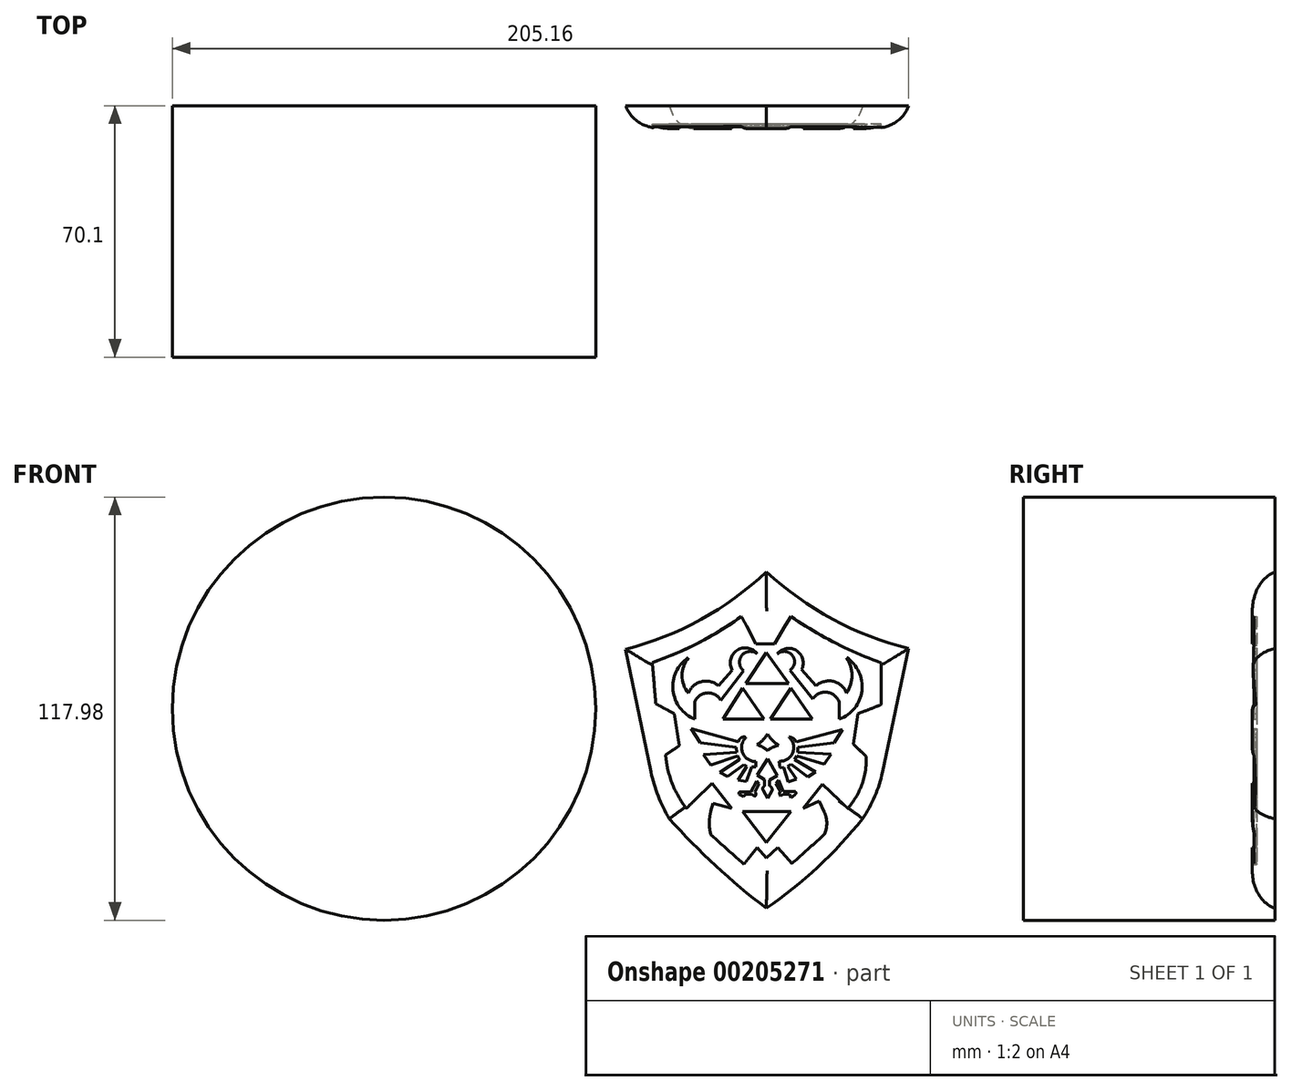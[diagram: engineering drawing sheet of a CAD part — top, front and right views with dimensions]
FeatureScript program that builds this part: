
annotation { "Feature Type Name" : "Feature", "Feature Type Description" : "" }
export const myFeature = defineFeature(function(context is Context, id is Id, definition is map)
    precondition{}
    {
        {
            var Q0;
            Q0=qCreatedBy(makeId("Front.planeOp"),FACE);
            var sketch = newSketch(context, id + "F0", { "sketchPlane" : qUnion([Q0])});
            skArc(sketch, "E0", {"start": v(0, 38.14) * mm, "mid": v(18.47, 24.95) * mm, "end": v(39.64, 16.77) * mm});
            skArc(sketch, "E1", {"start": v(-39.2, 16.56) * mm, "mid": v(-18.22, 24.85) * mm, "end": v(0, 38.14) * mm});
            skLineSegment(sketch, "E2", {"start": v(39.64, 16.77) * mm, "end": v(32.38, -17.63) * mm});
            skArc(sketch, "E3", {"start": v(26.82, -30.66) * mm, "mid": v(30.24, -24.41) * mm, "end": v(32.38, -17.63) * mm});
            skLineSegment(sketch, "E4", {"start": v(-39.2, 16.56) * mm, "end": v(-32.14, -17.63) * mm});
            skArc(sketch, "E5", {"start": v(-32.14, -17.63) * mm, "mid": v(-30.14, -24.36) * mm, "end": v(-27.02, -30.66) * mm});
            skArc(sketch, "E6", {"start": v(-27.02, -30.66) * mm, "mid": v(-14.13, -43.82) * mm, "end": v(0, -55.62) * mm});
            skArc(sketch, "E7", {"start": v(0, -55.62) * mm, "mid": v(14.35, -44.15) * mm, "end": v(26.82, -30.66) * mm});
            skLineSegment(sketch, "E8", {"start": v(0, 15.6) * mm, "end": v(6.22, 7.02) * mm});
            skLineSegment(sketch, "E9", {"start": v(6.22, 7.02) * mm, "end": v(-5.68, 7.02) * mm});
            skLineSegment(sketch, "E10", {"start": v(-5.68, 7.02) * mm, "end": v(0, 15.6) * mm});
            skLineSegment(sketch, "E11", {"start": v(6.82, 5.71) * mm, "end": v(12.77, -2.86) * mm});
            skLineSegment(sketch, "E12", {"start": v(12.77, -2.86) * mm, "end": v(1.18, -2.86) * mm});
            skLineSegment(sketch, "E13", {"start": v(1.18, -2.86) * mm, "end": v(6.82, 5.71) * mm});
            skLineSegment(sketch, "E14", {"start": v(-6.59, 5.71) * mm, "end": v(-0.64, -2.86) * mm});
            skLineSegment(sketch, "E15", {"start": v(-0.64, -2.86) * mm, "end": v(-12.03, -2.86) * mm});
            skLineSegment(sketch, "E16", {"start": v(-12.03, -2.86) * mm, "end": v(-6.59, 5.71) * mm});
            skLineSegment(sketch, "E17", {"start": v(6.82, -28.67) * mm, "end": v(0, -37.27) * mm});
            skLineSegment(sketch, "E18", {"start": v(0, -37.27) * mm, "end": v(-6.59, -28.67) * mm});
            skLineSegment(sketch, "E19", {"start": v(-6.59, -28.67) * mm, "end": v(6.82, -28.67) * mm});
            skArc(sketch, "E20", {"start": v(0.3, -7.06) * mm, "mid": v(1.7, -8.83) * mm, "end": v(3.44, -10.24) * mm});
            skArc(sketch, "E21", {"start": v(3.44, -10.24) * mm, "mid": v(1.8, -10.76) * mm, "end": v(0.3, -11.64) * mm});
            skArc(sketch, "E22", {"start": v(0.3, -11.64) * mm, "mid": v(-1.07, -10.72) * mm, "end": v(-2.6, -10.06) * mm});
            skArc(sketch, "E23", {"start": v(-2.6, -10.06) * mm, "mid": v(-0.95, -8.75) * mm, "end": v(0.3, -7.06) * mm});
            skArc(sketch, "E24", {"start": v(3.56, -14.66) * mm, "mid": v(7.35, -12.25) * mm, "end": v(6.28, -7.9) * mm});
            skLineSegment(sketch, "E25", {"start": v(3.56, -14.66) * mm, "end": v(3.83, -16.47) * mm});
            skLineSegment(sketch, "E26", {"start": v(3.83, -16.47) * mm, "end": v(4.79, -16.33) * mm});
            skLineSegment(sketch, "E27", {"start": v(4.79, -16.33) * mm, "end": v(6.13, -20.44) * mm});
            skLineSegment(sketch, "E28", {"start": v(6.13, -20.44) * mm, "end": v(8.33, -19.72) * mm});
            skLineSegment(sketch, "E29", {"start": v(8.33, -19.72) * mm, "end": v(5.9, -16.13) * mm});
            skLineSegment(sketch, "E30", {"start": v(5.9, -16.13) * mm, "end": v(6.88, -15.47) * mm});
            skLineSegment(sketch, "E31", {"start": v(6.88, -15.47) * mm, "end": v(11.5, -19) * mm});
            skLineSegment(sketch, "E32", {"start": v(11.5, -19) * mm, "end": v(13.74, -17.66) * mm});
            skLineSegment(sketch, "E33", {"start": v(13.74, -17.66) * mm, "end": v(7.9, -14.24) * mm});
            skLineSegment(sketch, "E34", {"start": v(7.9, -14.24) * mm, "end": v(8.55, -13.14) * mm});
            skLineSegment(sketch, "E35", {"start": v(8.55, -13.14) * mm, "end": v(16.18, -15.47) * mm});
            skLineSegment(sketch, "E36", {"start": v(16.18, -15.47) * mm, "end": v(18.03, -12.7) * mm});
            skLineSegment(sketch, "E37", {"start": v(18.03, -12.7) * mm, "end": v(8.78, -12.13) * mm});
            skLineSegment(sketch, "E38", {"start": v(8.78, -12.13) * mm, "end": v(8.78, -10.77) * mm});
            skLineSegment(sketch, "E39", {"start": v(8.78, -10.77) * mm, "end": v(18.97, -9.56) * mm});
            skLineSegment(sketch, "E40", {"start": v(18.97, -9.56) * mm, "end": v(21.16, -5.78) * mm});
            skLineSegment(sketch, "E41", {"start": v(21.16, -5.78) * mm, "end": v(8.33, -9.22) * mm});
            skArc(sketch, "E42", {"start": v(8.33, -9.22) * mm, "mid": v(7.48, -8.3) * mm, "end": v(6.28, -7.9) * mm});
            skLineSegment(sketch, "E43", {"start": v(0.4, -14) * mm, "end": v(3.07, -18.64) * mm});
            skLineSegment(sketch, "E44", {"start": v(3.07, -18.64) * mm, "end": v(0.93, -19.87) * mm});
            skLineSegment(sketch, "E45", {"start": v(0.93, -19.87) * mm, "end": v(0.93, -21.55) * mm});
            skLineSegment(sketch, "E46", {"start": v(0.4, -14) * mm, "end": v(-2.5, -18.52) * mm});
            skLineSegment(sketch, "E47", {"start": v(-2.5, -18.52) * mm, "end": v(-0.45, -19.84) * mm});
            skLineSegment(sketch, "E48", {"start": v(-0.45, -19.84) * mm, "end": v(-0.45, -21.55) * mm});
            skLineSegment(sketch, "E49", {"start": v(3.43, -19.87) * mm, "end": v(2.62, -20.77) * mm});
            skLineSegment(sketch, "E50", {"start": v(2.62, -20.77) * mm, "end": v(3.88, -22.96) * mm});
            skLineSegment(sketch, "E51", {"start": v(3.43, -19.87) * mm, "end": v(4.75, -23.1) * mm});
            skLineSegment(sketch, "E52", {"start": v(4.75, -23.1) * mm, "end": v(8.08, -23.1) * mm});
            skLineSegment(sketch, "E53", {"start": v(3.88, -24.34) * mm, "end": v(4.66, -23.83) * mm});
            skLineSegment(sketch, "E54", {"start": v(4.66, -23.83) * mm, "end": v(6.46, -23.83) * mm});
            skLineSegment(sketch, "E55", {"start": v(6.46, -23.83) * mm, "end": v(6.88, -24.82) * mm});
            skLineSegment(sketch, "E56", {"start": v(6.88, -24.82) * mm, "end": v(7.96, -24) * mm});
            skArc(sketch, "E57", {"start": v(7.96, -24) * mm, "mid": v(8.2, -23.58) * mm, "end": v(8.08, -23.1) * mm});
            skArc(sketch, "E58", {"start": v(1.58, -22.78) * mm, "mid": v(1.48, -22.04) * mm, "end": v(0.93, -21.55) * mm});
            skLineSegment(sketch, "E59", {"start": v(1.58, -22.78) * mm, "end": v(0.4, -25.04) * mm});
            skLineSegment(sketch, "E60", {"start": v(0.4, -25.04) * mm, "end": v(-0.9, -22.78) * mm});
            skArc(sketch, "E61", {"start": v(-0.45, -21.55) * mm, "mid": v(-0.96, -22.06) * mm, "end": v(-0.9, -22.78) * mm});
            skArc(sketch, "E62", {"start": v(-5.7, -7.99) * mm, "mid": v(-6.6, -12.34) * mm, "end": v(-2.89, -14.76) * mm});
            skArc(sketch, "E63", {"start": v(-5.7, -7.99) * mm, "mid": v(-7.02, -8.13) * mm, "end": v(-7.74, -9.24) * mm});
            skLineSegment(sketch, "E64", {"start": v(-2.89, -14.76) * mm, "end": v(-2.89, -16.26) * mm});
            skPoint(sketch, "E64.endSnap0", {"position": v(-1.05, -16.26) * mm});
            skLineSegment(sketch, "E65", {"start": v(-2.89, -16.26) * mm, "end": v(-4.14, -16.26) * mm});
            skLineSegment(sketch, "E66", {"start": v(-4.14, -16.26) * mm, "end": v(-5.63, -20.36) * mm});
            skLineSegment(sketch, "E67", {"start": v(-5.63, -20.36) * mm, "end": v(-7.88, -19.9) * mm});
            skLineSegment(sketch, "E68", {"start": v(-7.88, -19.9) * mm, "end": v(-5.41, -16.05) * mm});
            skLineSegment(sketch, "E69", {"start": v(-5.41, -16.05) * mm, "end": v(-6.2, -15.55) * mm});
            skLineSegment(sketch, "E70", {"start": v(-6.2, -15.55) * mm, "end": v(-10.77, -18.93) * mm});
            skLineSegment(sketch, "E71", {"start": v(-10.77, -18.93) * mm, "end": v(-13.01, -17.83) * mm});
            skLineSegment(sketch, "E72", {"start": v(-13.01, -17.83) * mm, "end": v(-7.45, -14.2) * mm});
            skLineSegment(sketch, "E73", {"start": v(-7.99, -13.16) * mm, "end": v(-15.54, -15.72) * mm});
            skLineSegment(sketch, "E74", {"start": v(-15.54, -15.72) * mm, "end": v(-17.58, -12.87) * mm});
            skLineSegment(sketch, "E75", {"start": v(-17.58, -12.87) * mm, "end": v(-8.27, -12.16) * mm});
            skLineSegment(sketch, "E76", {"start": v(-8.27, -12.16) * mm, "end": v(-8.38, -10.8) * mm});
            skLineSegment(sketch, "E77", {"start": v(-8.38, -10.8) * mm, "end": v(-18.4, -9.56) * mm});
            skLineSegment(sketch, "E78", {"start": v(-18.4, -9.56) * mm, "end": v(-20.97, -5.62) * mm});
            skLineSegment(sketch, "E79", {"start": v(-20.97, -5.62) * mm, "end": v(-7.74, -9.24) * mm});
            skArc(sketch, "E80", {"start": v(-7.99, -13.16) * mm, "mid": v(-7.75, -13.69) * mm, "end": v(-7.45, -14.2) * mm});
            skLineSegment(sketch, "E81", {"start": v(-2.69, -20.14) * mm, "end": v(-2.05, -20.98) * mm});
            skLineSegment(sketch, "E82", {"start": v(-2.05, -20.98) * mm, "end": v(-3.22, -23.19) * mm});
            skLineSegment(sketch, "E83", {"start": v(-2.69, -20.14) * mm, "end": v(-4.3, -23.19) * mm});
            skLineSegment(sketch, "E84", {"start": v(-4.3, -23.19) * mm, "end": v(-7.2, -23.19) * mm});
            skArc(sketch, "E85", {"start": v(-3.22, -24.52) * mm, "mid": v(-2.93, -23.86) * mm, "end": v(-3.22, -23.19) * mm});
            skLineSegment(sketch, "E86", {"start": v(-3.22, -24.52) * mm, "end": v(-4.09, -23.86) * mm});
            skLineSegment(sketch, "E87", {"start": v(-4.09, -23.86) * mm, "end": v(-5.74, -23.86) * mm});
            skLineSegment(sketch, "E88", {"start": v(-5.74, -23.86) * mm, "end": v(-6.42, -24.52) * mm});
            skLineSegment(sketch, "E89", {"start": v(-6.42, -24.52) * mm, "end": v(-7.6, -23.86) * mm});
            skArc(sketch, "E90", {"start": v(3.88, -22.96) * mm, "mid": v(3.7, -23.65) * mm, "end": v(3.88, -24.34) * mm});
            skArc(sketch, "E91", {"start": v(-7.2, -23.19) * mm, "mid": v(-7.6, -23.4) * mm, "end": v(-7.6, -23.86) * mm});
            skLineSegment(sketch, "E92", {"start": v(-6.96, 25.7) * mm, "end": v(-2.88, 18.02) * mm});
            skLineSegment(sketch, "E93", {"start": v(-2.88, 18.02) * mm, "end": v(2.28, 18.02) * mm});
            skLineSegment(sketch, "E94", {"start": v(2.28, 18.02) * mm, "end": v(6.83, 25.7) * mm});
            skArc(sketch, "E95", {"start": v(6.83, 25.7) * mm, "mid": v(19, 18.4) * mm, "end": v(32.01, 12.75) * mm});
            skLineSegment(sketch, "E96", {"start": v(32.01, 12.75) * mm, "end": v(32.01, 1.12) * mm});
            skLineSegment(sketch, "E97", {"start": v(32.01, 1.12) * mm, "end": v(25.54, -1.4) * mm});
            skLineSegment(sketch, "E98", {"start": v(25.54, -1.4) * mm, "end": v(24.22, -9.91) * mm});
            skLineSegment(sketch, "E99", {"start": v(24.22, -9.91) * mm, "end": v(27.82, -13.27) * mm});
            skArc(sketch, "E100", {"start": v(-31.78, 12.87) * mm, "mid": v(-18.89, 18.36) * mm, "end": v(-6.96, 25.7) * mm});
            skLineSegment(sketch, "E101", {"start": v(-31.78, 12.87) * mm, "end": v(-30.82, 1.36) * mm});
            skLineSegment(sketch, "E102", {"start": v(-30.82, 1.36) * mm, "end": v(-25.66, -1.4) * mm});
            skLineSegment(sketch, "E103", {"start": v(-25.66, -1.4) * mm, "end": v(-24.22, -10.27) * mm});
            skLineSegment(sketch, "E104", {"start": v(-24.22, -10.27) * mm, "end": v(-28.06, -12.91) * mm});
            skArc(sketch, "E105", {"start": v(-28.06, -12.91) * mm, "mid": v(-26.28, -20.77) * mm, "end": v(-22.3, -27.78) * mm});
            skArc(sketch, "E106", {"start": v(22.66, -27.78) * mm, "mid": v(26.65, -21.03) * mm, "end": v(27.82, -13.27) * mm});
            skLineSegment(sketch, "E107", {"start": v(22.66, -27.78) * mm, "end": v(15.59, -21.06) * mm});
            skLineSegment(sketch, "E108", {"start": v(15.59, -21.06) * mm, "end": v(10.3, -27.78) * mm});
            skLineSegment(sketch, "E109", {"start": v(10.3, -27.78) * mm, "end": v(14.75, -25.74) * mm});
            skLineSegment(sketch, "E110", {"start": v(14.75, -25.74) * mm, "end": v(16.14, -28.77) * mm});
            skLineSegment(sketch, "E111", {"start": v(-22.3, -27.78) * mm, "end": v(-15.11, -20.83) * mm});
            skLineSegment(sketch, "E112", {"start": v(-15.11, -20.83) * mm, "end": v(-9.6, -27.78) * mm});
            skLineSegment(sketch, "E113", {"start": v(-9.6, -27.78) * mm, "end": v(-14.84, -26.35) * mm});
            skLineSegment(sketch, "E114", {"start": v(-14.84, -26.35) * mm, "end": v(-15.46, -28.6) * mm});
            skArc(sketch, "E115", {"start": v(-15.46, -28.6) * mm, "mid": v(-15.9, -31.89) * mm, "end": v(-15.46, -35.17) * mm});
            skArc(sketch, "E116", {"start": v(16.14, -35.1) * mm, "mid": v(16.83, -31.93) * mm, "end": v(16.14, -28.77) * mm});
            skLineSegment(sketch, "E117", {"start": v(16.14, -35.1) * mm, "end": v(7.15, -43.16) * mm});
            skLineSegment(sketch, "E118", {"start": v(7.15, -43.16) * mm, "end": v(3.2, -38.75) * mm});
            skLineSegment(sketch, "E119", {"start": v(3.2, -38.75) * mm, "end": v(0, -41.61) * mm});
            skLineSegment(sketch, "E120", {"start": v(0, -41.61) * mm, "end": v(-2.57, -38.75) * mm});
            skLineSegment(sketch, "E121", {"start": v(-2.57, -38.75) * mm, "end": v(-6.26, -43.37) * mm});
            skLineSegment(sketch, "E122", {"start": v(-6.26, -43.37) * mm, "end": v(-15.46, -35.17) * mm});
            skPoint(sketch, "E123.endSnap0", {"position": v(-12.36, -24.3) * mm});
            skLineSegment(sketch, "E124", {"start": v(-9.5, 10.75) * mm, "end": v(-13.34, 6.35) * mm});
            skLineSegment(sketch, "E125", {"start": v(9.82, 10.9) * mm, "end": v(13.88, 6.35) * mm});
            skLineSegment(sketch, "E126", {"start": v(6.56, 10.64) * mm, "end": v(12.9, 2.63) * mm});
            skLineSegment(sketch, "E127", {"start": v(20.34, 1.56) * mm, "end": v(20.34, -2.92) * mm});
            skLineSegment(sketch, "E128", {"start": v(-19.93, 1.94) * mm, "end": v(-19.93, -2.92) * mm});
            skLineSegment(sketch, "E129", {"start": v(-6.3, 10.54) * mm, "end": v(-12.72, 2.36) * mm});
            skArc(sketch, "E130", {"start": v(-12.72, 2.36) * mm, "mid": v(-16.46, 4.4) * mm, "end": v(-19.93, 1.94) * mm});
            skArc(sketch, "E131", {"start": v(-13.34, 6.35) * mm, "mid": v(-18.08, 7.52) * mm, "end": v(-21.74, 4.29) * mm});
            skArc(sketch, "E132", {"start": v(-21.74, 14.22) * mm, "mid": v(-23.49, 9.25) * mm, "end": v(-21.74, 4.29) * mm});
            skArc(sketch, "E133", {"start": v(-21.74, 14.22) * mm, "mid": v(-26, 5.1) * mm, "end": v(-19.93, -2.92) * mm});
            skArc(sketch, "E134", {"start": v(22.37, 4.29) * mm, "mid": v(18.68, 7.59) * mm, "end": v(13.88, 6.35) * mm});
            skArc(sketch, "E135", {"start": v(20.34, 1.56) * mm, "mid": v(16.97, 4.53) * mm, "end": v(12.9, 2.63) * mm});
            skArc(sketch, "E136", {"start": v(22.37, 4.29) * mm, "mid": v(23.83, 9.25) * mm, "end": v(22.37, 14.22) * mm});
            skArc(sketch, "E137", {"start": v(20.34, -2.92) * mm, "mid": v(26.6, 5.03) * mm, "end": v(22.37, 14.22) * mm});
            skArc(sketch, "E138", {"start": v(9.82, 10.9) * mm, "mid": v(8.44, 16.14) * mm, "end": v(3.1, 15.29) * mm});
            skArc(sketch, "E139", {"start": v(6.56, 10.64) * mm, "mid": v(7.27, 14.8) * mm, "end": v(3.1, 15.29) * mm});
            skArc(sketch, "E140", {"start": v(-2.57, 15.29) * mm, "mid": v(-6.85, 14.8) * mm, "end": v(-6.3, 10.54) * mm});
            skArc(sketch, "E141", {"start": v(-2.57, 15.29) * mm, "mid": v(-8.16, 16.26) * mm, "end": v(-9.5, 10.75) * mm});
            skCircle(sketch, "E142", {"center": v(-106.54, 0) * mm, "radius": 58.99 * mm});
            skSolve(sketch);
        }
        {
            var Q0;
            Q0=makeQuery(id+"F0.imprint","IMPRINT",FACE,{"disambiguationData":[TD([[makeQuery(id+"F0.imprint","IMPRINT",EDGE,{"derivedFrom":sQuery(id+"F0.wireOp",EDGE,"E0")}),-1.0]])]});
            extrude(context, id + "F1", {"entities" : qUnion([Q0]), "depth" : 6.35 * mm});
        }
        {
            var Q0;
            Q0=makeQuery(id+"F0.imprint","IMPRINT",FACE,{"disambiguationData":[TD([[makeQuery(id+"F0.imprint","IMPRINT",EDGE,{"derivedFrom":sQuery(id+"F0.wireOp",EDGE,"E8")}),1.0]])]});
            extrude(context, id + "F2", {"entities" : qUnion([Q0]), "operationType" : NewBodyOperationType.ADD, "depth" : 5.08 * mm});
        }
        {
            var Q0;
            Q0=makeQuery(id+"F0.imprint","IMPRINT",FACE,{"disambiguationData":[TD([[makeQuery(id+"F0.imprint","IMPRINT",EDGE,{"derivedFrom":sQuery(id+"F0.wireOp",EDGE,"E11")}),-1.0]])]});
            var Q1;
            Q1=makeQuery(id+"F0.imprint","IMPRINT",FACE,{"disambiguationData":[TD([[makeQuery(id+"F0.imprint","IMPRINT",EDGE,{"derivedFrom":sQuery(id+"F0.wireOp",EDGE,"E8")}),-1.0]])]});
            var Q2;
            Q2=makeQuery(id+"F0.imprint","IMPRINT",FACE,{"disambiguationData":[TD([[makeQuery(id+"F0.imprint","IMPRINT",EDGE,{"derivedFrom":sQuery(id+"F0.wireOp",EDGE,"E14")}),-1.0]])]});
            extrude(context, id + "F3", {"entities" : qUnion([Q0, Q1, Q2]), "operationType" : NewBodyOperationType.ADD, "depth" : 5.84 * mm});
        }
        {
            var Q0;
            Q0=makeQuery(id+"F0.imprint","IMPRINT",FACE,{"disambiguationData":[TD([[makeQuery(id+"F0.imprint","IMPRINT",EDGE,{"derivedFrom":sQuery(id+"F0.wireOp",EDGE,"E125")}),-1.0]])]});
            var Q1;
            Q1=makeQuery(id+"F0.imprint","IMPRINT",FACE,{"disambiguationData":[TD([[makeQuery(id+"F0.imprint","IMPRINT",EDGE,{"derivedFrom":sQuery(id+"F0.wireOp",EDGE,"E124")}),1.0]])]});
            var Q2;
            Q2=makeQuery(id+"F0.imprint","IMPRINT",FACE,{"disambiguationData":[TD([[makeQuery(id+"F0.imprint","IMPRINT",EDGE,{"derivedFrom":sQuery(id+"F0.wireOp",EDGE,"E62")}),-1.0]])]});
            var Q3;
            Q3=makeQuery(id+"F0.imprint","IMPRINT",FACE,{"disambiguationData":[TD([[makeQuery(id+"F0.imprint","IMPRINT",EDGE,{"derivedFrom":sQuery(id+"F0.wireOp",EDGE,"E43")}),-1.0]])]});
            var Q4;
            Q4=makeQuery(id+"F0.imprint","IMPRINT",FACE,{"disambiguationData":[TD([[makeQuery(id+"F0.imprint","IMPRINT",EDGE,{"derivedFrom":sQuery(id+"F0.wireOp",EDGE,"E24")}),-1.0]])]});
            var Q5;
            Q5=makeQuery(id+"F0.imprint","IMPRINT",FACE,{"disambiguationData":[TD([[makeQuery(id+"F0.imprint","IMPRINT",EDGE,{"derivedFrom":sQuery(id+"F0.wireOp",EDGE,"E20")}),-1.0]])]});
            var Q6;
            Q6=makeQuery(id+"F0.imprint","IMPRINT",FACE,{"disambiguationData":[TD([[makeQuery(id+"F0.imprint","IMPRINT",EDGE,{"derivedFrom":sQuery(id+"F0.wireOp",EDGE,"E17")}),-1.0]])]});
            var Q7;
            Q7=makeQuery(id+"F0.imprint","IMPRINT",FACE,{"disambiguationData":[TD([[makeQuery(id+"F0.imprint","IMPRINT",EDGE,{"derivedFrom":sQuery(id+"F0.wireOp",EDGE,"E49")}),1.0]])]});
            var Q8;
            Q8=makeQuery(id+"F0.imprint","IMPRINT",FACE,{"disambiguationData":[TD([[makeQuery(id+"F0.imprint","IMPRINT",EDGE,{"derivedFrom":sQuery(id+"F0.wireOp",EDGE,"E81")}),-1.0]])]});
            extrude(context, id + "F4", {"entities" : qUnion([Q0, Q1, Q2, Q3, Q4, Q5, Q6, Q7, Q8]), "operationType" : NewBodyOperationType.ADD, "depth" : 5.84 * mm});
        }
        {
            var Q0;
            Q0=makeQuery(id+"F1.opExtrude","CAP_EDGE",EDGE,{"disambiguationData":[OSD([sQuery(id+"F0.wireOp",EDGE,"E6")])],"isStart":false});
            var Q1;
            Q1=makeQuery(id+"F1.opExtrude","CAP_EDGE",EDGE,{"disambiguationData":[OSD([sQuery(id+"F0.wireOp",EDGE,"E7")])],"isStart":false});
            var Q2;
            Q2=makeQuery(id+"F1.opExtrude","CAP_EDGE",EDGE,{"disambiguationData":[OSD([sQuery(id+"F0.wireOp",EDGE,"E3")])],"isStart":false});
            var Q3;
            Q3=makeQuery(id+"F1.opExtrude","CAP_EDGE",EDGE,{"disambiguationData":[OSD([sQuery(id+"F0.wireOp",EDGE,"E2")])],"isStart":false});
            var Q4;
            Q4=makeQuery(id+"F1.opExtrude","CAP_EDGE",EDGE,{"disambiguationData":[OSD([sQuery(id+"F0.wireOp",EDGE,"E0")])],"isStart":false});
            var Q5;
            Q5=makeQuery(id+"F1.opExtrude","CAP_EDGE",EDGE,{"disambiguationData":[OSD([sQuery(id+"F0.wireOp",EDGE,"E1")])],"isStart":false});
            var Q6;
            Q6=makeQuery(id+"F1.opExtrude","CAP_EDGE",EDGE,{"disambiguationData":[OSD([sQuery(id+"F0.wireOp",EDGE,"E4")])],"isStart":false});
            var Q7;
            Q7=makeQuery(id+"F1.opExtrude","CAP_EDGE",EDGE,{"disambiguationData":[OSD([sQuery(id+"F0.wireOp",EDGE,"E5")])],"isStart":false});
            fillet(context, id + "F5", {"entities" : qUnion([Q0, Q1, Q2, Q3, Q4, Q5, Q6, Q7]), "radius" : 8.58 * mm, "tangentPropagation" : true, "allowEdgeOverflow" : false});
        }
        {
            var Q0;
            Q0=makeQuery(id+"F0.imprint","IMPRINT",FACE,{"disambiguationData":[TD([[makeQuery(id+"F0.imprint","IMPRINT",EDGE,{"derivedFrom":sQuery(id+"F0.wireOp",EDGE,"E142")}),1.0]])]});
            extrude(context, id + "F6", {"entities" : qUnion([Q0]), "depth" : 70.1 * mm, "offsetDistance" : 25.4 * mm});
        }
    });
